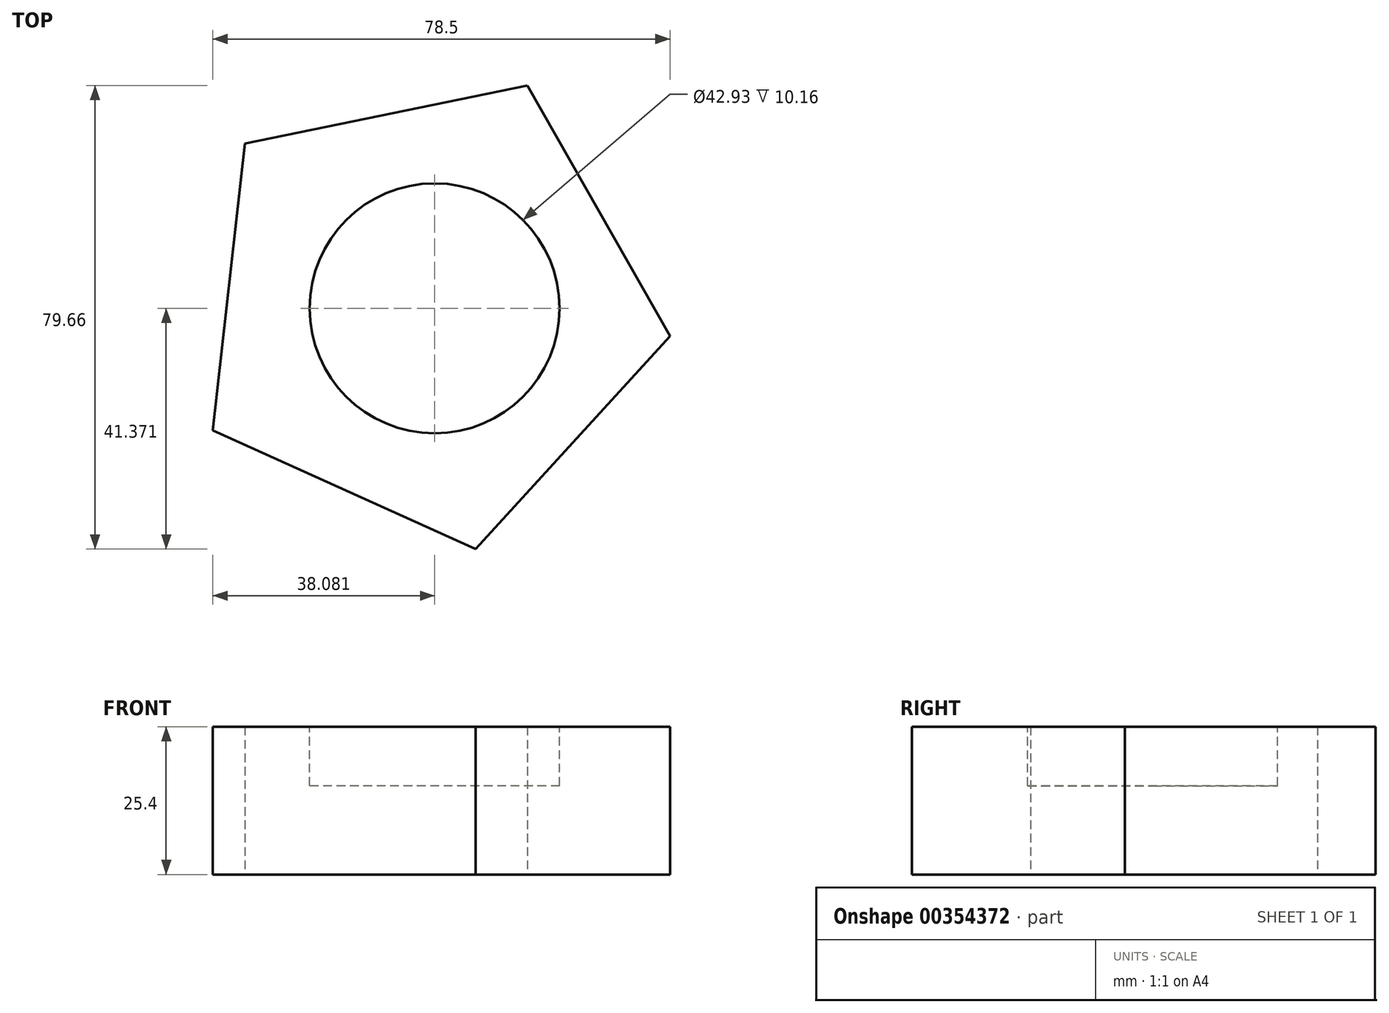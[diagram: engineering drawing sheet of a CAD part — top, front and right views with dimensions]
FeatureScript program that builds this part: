
annotation { "Feature Type Name" : "Feature", "Feature Type Description" : "" }
export const myFeature = defineFeature(function(context is Context, id is Id, definition is map)
    precondition{}
    {
        {
            var Q0;
            Q0=qCreatedBy(makeId("Top.planeOp"),FACE);
            var sketch = newSketch(context, id + "F0", { "sketchPlane" : qUnion([Q0])});
            skCircle(sketch, "E0.cCircle", {"center": v(0, 0) * mm, "radius": 34.1 * mm, "construction": true});
            skLineSegment(sketch, "E0.0", {"start": v(41.88, -4.66) * mm, "end": v(8.51, -41.27) * mm});
            skLineSegment(sketch, "E0.1", {"start": v(8.51, -41.27) * mm, "end": v(-36.62, -20.85) * mm});
            skLineSegment(sketch, "E0.2", {"start": v(-36.62, -20.85) * mm, "end": v(-31.15, 28.39) * mm});
            skLineSegment(sketch, "E0.3", {"start": v(-31.15, 28.39) * mm, "end": v(17.37, 38.4) * mm});
            skLineSegment(sketch, "E0.4", {"start": v(17.37, 38.4) * mm, "end": v(41.88, -4.66) * mm});
            skPoint(sketch, "E0.0.midPoint", {"position": v(25.2, -22.97) * mm});
            skSolve(sketch);
        }
        {
            var Q0;
            Q0 = qSketchRegion(id + "F0", true);
            extrude(context, id + "F1", {"entities" : qUnion([Q0]), "depth" : 25.4 * mm});
        }
        {
            var Q0;
            Q0=makeQuery(id+"F1.opExtrude","CAP_FACE",FACE,{"disambiguationData":[OSD([sQuery(id+"F0.wireOp",EDGE,"E0.0"),sQuery(id+"F0.wireOp",EDGE,"E0.1"),sQuery(id+"F0.wireOp",EDGE,"E0.2"),sQuery(id+"F0.wireOp",EDGE,"E0.3"),sQuery(id+"F0.wireOp",EDGE,"E0.4")])],"isStart":false});
            var sketch = newSketch(context, id + "F2", { "sketchPlane" : qUnion([Q0])});
            skCircle(sketch, "E1", {"center": v(1.46, 0.1) * mm, "radius": 21.47 * mm});
            skPoint(sketch, "E1.first.point", {"position": v(-15.73, 12.96) * mm});
            skPoint(sketch, "E1.second.point", {"position": v(22.18, -5.5) * mm});
            skPoint(sketch, "E1.third.point", {"position": v(0, -21.32) * mm});
            skSolve(sketch);
        }
        {
            var Q0;
            Q0=makeQuery(id+"F2.imprint","IMPRINT",FACE,{"disambiguationData":[TD([[makeQuery(id+"F2.imprint","IMPRINT",EDGE,{"derivedFrom":sQuery(id+"F2.wireOp",EDGE,"E1")}),1.0]])]});
            var Q1;
            Q1=sQuery(id+"F2.wireOp",EDGE,"E1");
            extrude(context, id + "F3", {"entities" : qUnion([Q0]), "operationType" : NewBodyOperationType.REMOVE, "surfaceEntities" : qUnion([Q1]), "endBound" : BoundingType.SYMMETRIC, "oppositeDirection" : true, "depth" : 20.32 * mm});
        }
    });
